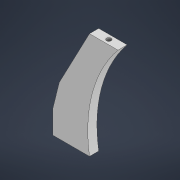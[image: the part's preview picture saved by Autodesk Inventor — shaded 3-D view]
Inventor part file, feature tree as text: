
AUTODESK INVENTOR PART (.ipt)
format: ipt  version: 2022 (Build 260153000, 153)  size: 108,544 bytes
history: native  units: in
note: dims shown in document units (in); Inventor stores cm internally (conversion verified against a paired STEP export)
features: extrude x2, sketch x2, chamfer x1
ambient origin geometry x8: Origin, YZ Plane, XZ Plane, XY Plane, X Axis, Y Axis, Z Axis, Center Point
bodies: Solid1 (feature_tree)
feature tree (5):
  extrude  "Extrusion1"  Depth=3.1496in
  chamfer  "Chamfer1"  Distance=0.7874in
  extrude  "Extrusion2"  Depth=0.3937in
  sketch  "Sketch1"  dims[d2=9.4488in d4=3.1496in d5=0.7874in d6=0.0in]
  sketch  "Sketch2"  dims[d7=1.1811in d8=0.0787in d9=45.0deg d10=1.1811in d11=0.3937in d12=0.3937in d13=0.0in]
